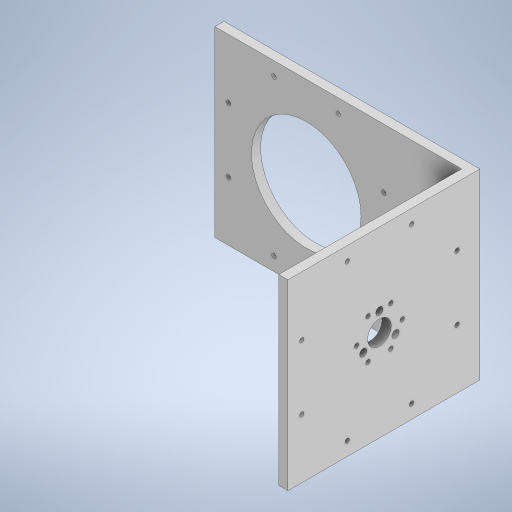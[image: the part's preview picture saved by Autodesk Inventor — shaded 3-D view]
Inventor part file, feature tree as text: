
AUTODESK INVENTOR PART (.ipt)
format: ipt  version: 2024.3 (Build 283343000, 343)  size: 315,392 bytes
history: native  units: mm
features: sketch x8, extrude x5, hole x3, other x1
ambient origin geometry x8: Origin, YZ Plane, XZ Plane, XY Plane, X Axis, Y Axis, Z Axis, Center Point
bodies: Body1 (feature_tree)
feature tree (17):
  other  "ソリッド1"
  extrude  "押し出し1"  Depth=97.0mm
  hole  "穴1"  [1 undecoded]
  extrude  "押し出し2"  Depth=50.0mm
  extrude  "押し出し3"  Depth=50.0mm
  extrude  "押し出し4"  Depth=50.0mm
  hole  "穴2"  [1 undecoded]
  hole  "穴3"  [1 undecoded]
  extrude  "押し出し5"  TaperAngle=22.5deg  [1 undecoded]
  sketch  "スケッチ1"
  sketch  "スケッチ2"
  sketch  "スケッチ3"
  sketch  "スケッチ4"
  sketch  "スケッチ5"
  sketch  "スケッチ6"
  sketch  "スケッチ7"
  sketch  "スケッチ8"
note: 4 required parameter values undecoded (feature->parameter linkage not recoverable at this tier; creation-order binding heuristic only, values carry confidence <= 0.55)
